# Revit family: Kitchen_Taps-Mixers_hansgrohe_74810XXX-Zesis-M33-Single-lever-kitchen_21
name_source: partatom
category: Plumbing Fixtures
revit_build: Autodesk Revit 2018 (Build: 20170223_1515(x64)
units: mm (PartAtom-declared; Revit-internal decimal feet)

## family parameters
Always vertical = No
Cut with Voids When Loaded = No
OmniClass Number = 23.45.55.17
OmniClass Title = Mixing Faucets
Part Type = Normal
Room Calculation Point = No
Round Connector Dimension = Use Diameter
Shared = No
Work Plane-Based = Yes

## types (1)
- 000 Chrome
    Always visible = Yes
    BIMobject category = Taps & Mixers
    Cold Water Inlet = 10 mm
    Cold Water Inlet Description = Cold Water Inlet 9.5 mm
    Default Elevation = 1219.2 mm  [stored 4 ft]
    Description = Zesis M33 Single lever kitchen mixer 150, Eco, pull-out spray, 2jet
    Design country = Germany
    Edition number = 1
    Hot Water Inlet = 10 mm
    Hot Water Inlet Description = Hot Water Inlet 9.5 mm
    IFC Classification = Valve
    Manufacturer = Hansgrohe
    Manufacturer country = Germany
    Manufacturer name = hansgrohe
    Masterformat 2014 Code = 22 41 39
    Masterformat 2014 Description = Residential Faucets, Supplies, and Trim
    Material 1 = Hansgrohe - Metal - 000 Chrome
    Model = 74810XXX
    OmniClass Code = 23-31 11 15 11
    OmniClass Description = Sink Cartridge Faucets
    Product Guid = c9a0aa6e-2329-4185-8500-09c26168be79
    Product SKU = 74810XXX
    Product data url = https://www.bimobject.com
    Product family = Zesis M33
    Product group = Kitchen mixers
    Product name = 74810XXX Zesis M33 Single lever kitchen mixer 150, Eco, pull-out spray, 2jet
    QR code = https://www.bimobject.com
    URL = https://www.hansgrohe.com
    Uniclass 2015 Code = Pr_40_20_87_84
    Uniclass 2015 Name = Sink taps
    Uniformat II Code = D2010
    Uniformat II Description = Plumbing Fixtures
    Weight Net (Kg) = 1.9

note: [stored X ft] marks values corroborated as IEEE doubles in the binary element streams (Revit-internal decimal feet)

## geometry (parser evidence)
native form markers: Sweep x1
no freeform markers — native parametric forms only
